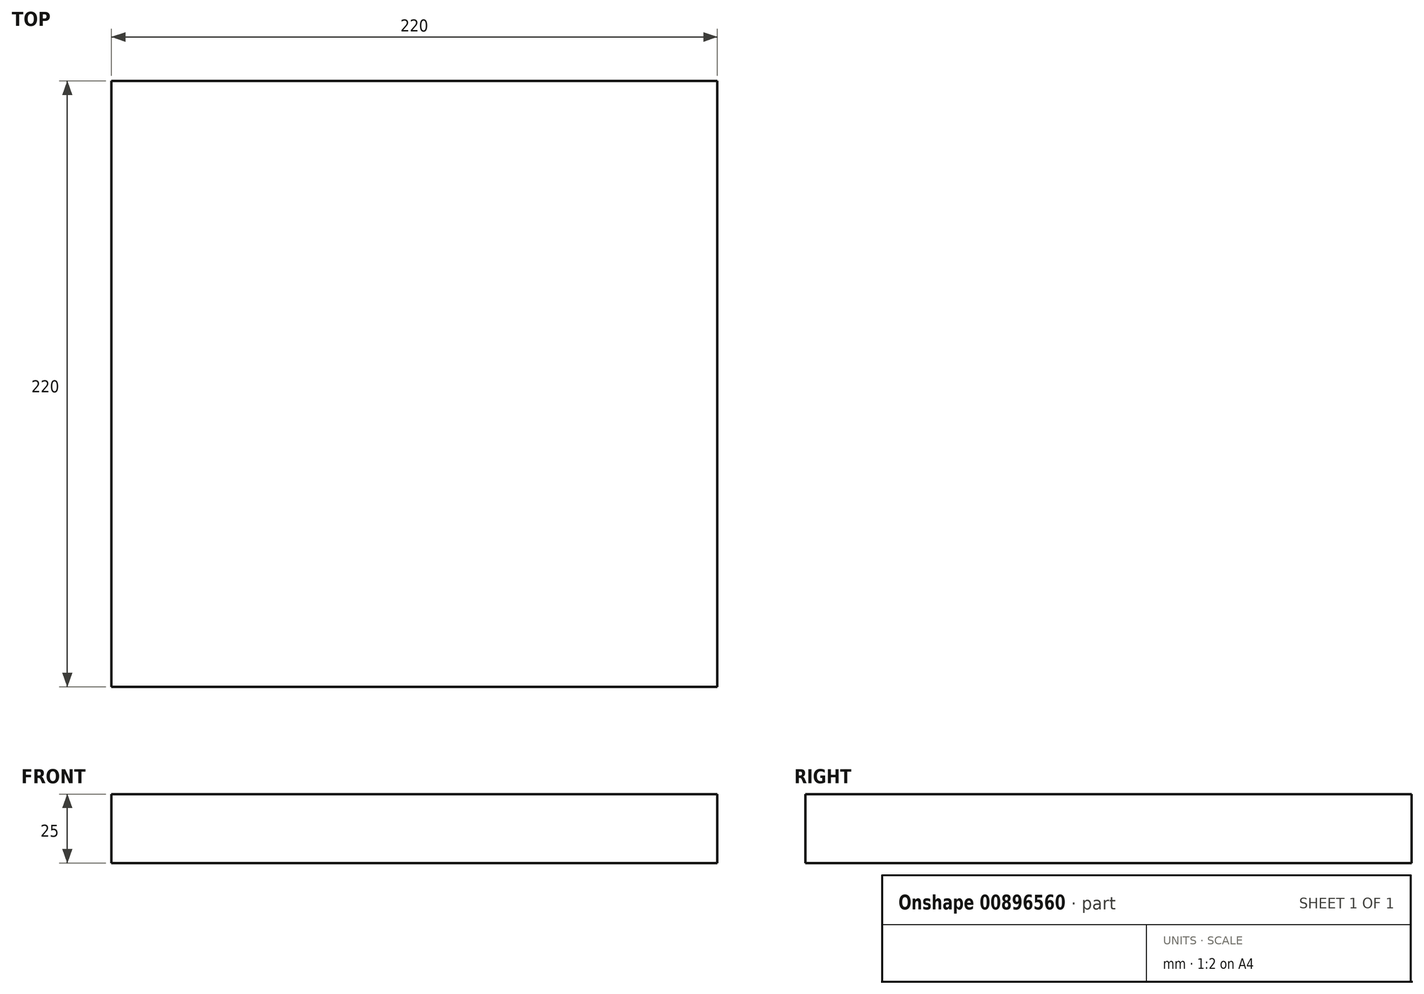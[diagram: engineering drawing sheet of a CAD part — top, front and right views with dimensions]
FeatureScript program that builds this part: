
annotation { "Feature Type Name" : "Feature", "Feature Type Description" : "" }
export const myFeature = defineFeature(function(context is Context, id is Id, definition is map)
    precondition{}
    {
        {
            var Q0;
            Q0=qCreatedBy(makeId("Top.planeOp"),FACE);
            var sketch = newSketch(context, id + "F0", { "sketchPlane" : qUnion([Q0])});
            skLineSegment(sketch, "E0.bottom", {"start": v(-109.1, 109.97) * mm, "end": v(110.9, 109.97) * mm});
            skLineSegment(sketch, "E0.top", {"start": v(-109.1, -110.03) * mm, "end": v(110.9, -110.03) * mm});
            skLineSegment(sketch, "E0.left", {"start": v(-109.1, 109.97) * mm, "end": v(-109.1, -110.03) * mm});
            skLineSegment(sketch, "E0.right", {"start": v(110.9, 109.97) * mm, "end": v(110.9, -110.03) * mm});
            skSolve(sketch);
        }
        {
            var Q0;
            Q0 = qSketchRegion(id + "F0", true);
            extrude(context, id + "F1", {"entities" : qUnion([Q0]), "depth" : 25 * mm, "offsetDistance" : 25 * mm});
        }
    });
